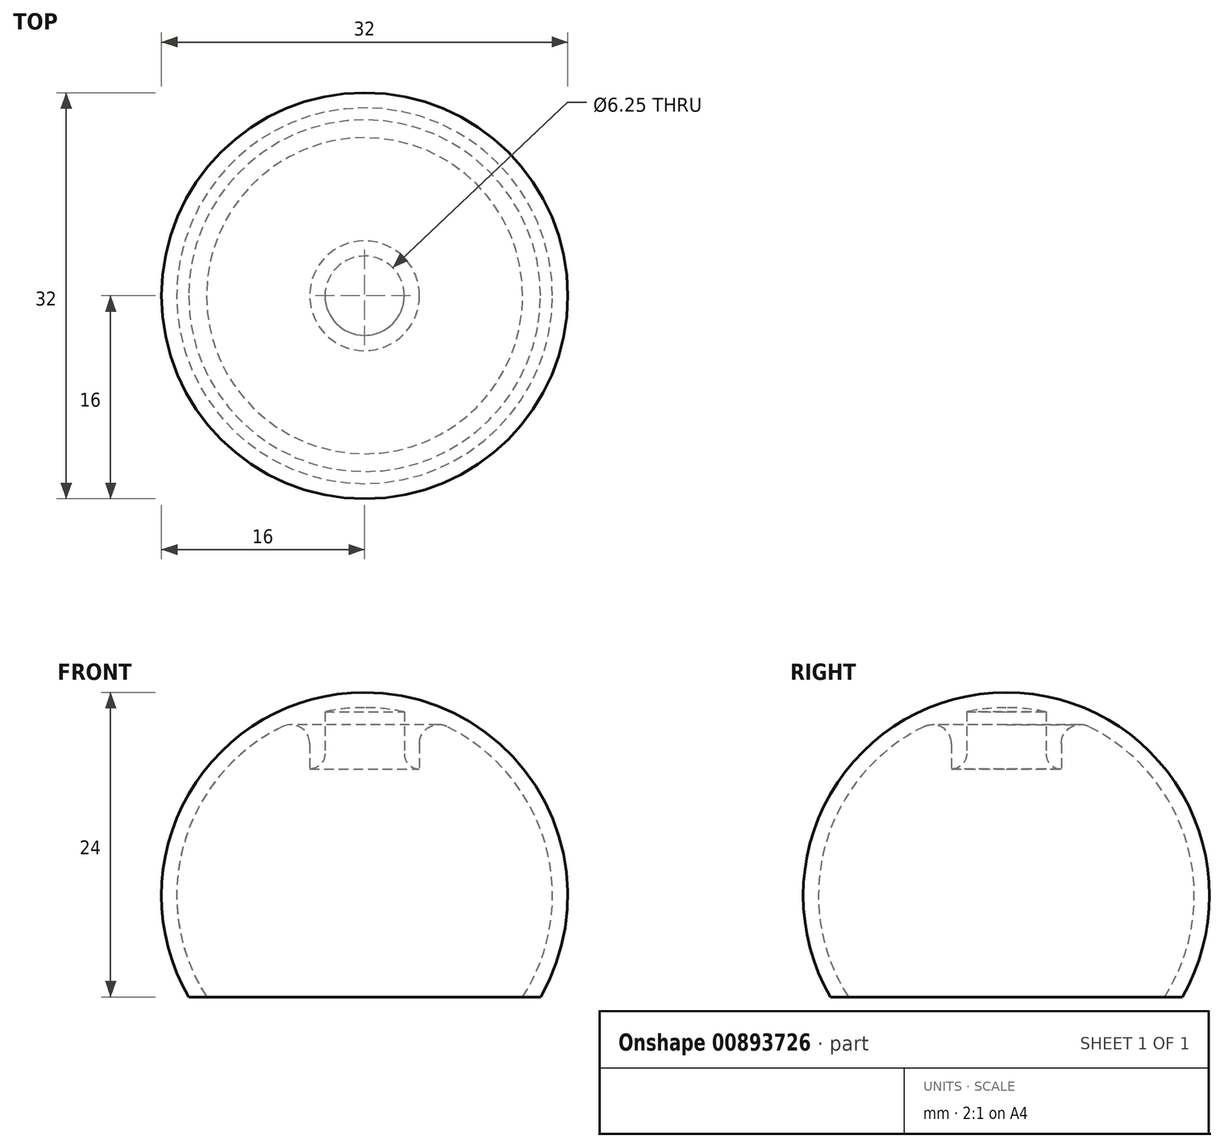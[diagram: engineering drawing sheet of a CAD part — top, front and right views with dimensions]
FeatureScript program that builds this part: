
annotation { "Feature Type Name" : "Feature", "Feature Type Description" : "" }
export const myFeature = defineFeature(function(context is Context, id is Id, definition is map)
    precondition{}
    {
        {
            var Q0;
            Q0=qCreatedBy(makeId("Front.planeOp"),FACE);
            var sketch = newSketch(context, id + "F0", { "sketchPlane" : qUnion([Q0])});
            skArc(sketch, "E0", {"start": v(0, 24) * mm, "mid": v(-13.86, 16) * mm, "end": v(-13.86, 0) * mm});
            skPoint(sketch, "E1", {"position": v(0, 24) * mm});
            skArc(sketch, "E2.0", {"start": v(0, 22.8) * mm, "mid": v(-12.99, 15.1) * mm, "end": v(-12.45, 0) * mm});
            skLineSegment(sketch, "E3", {"start": v(-13.86, 0) * mm, "end": v(-12.45, 0) * mm});
            skPoint(sketch, "E4.orphan", {"position": v(12.45, 0) * mm});
            skPoint(sketch, "E5.orphan", {"position": v(13.86, 0) * mm});
            skLineSegment(sketch, "E6", {"start": v(-4.32, 22.15) * mm, "end": v(-4.32, 17.97) * mm});
            skLineSegment(sketch, "E7", {"start": v(-4.32, 17.97) * mm, "end": v(-3.12, 17.97) * mm});
            skLineSegment(sketch, "E8", {"start": v(-3.12, 17.97) * mm, "end": v(-3.13, 22.47) * mm});
            skLineSegment(sketch, "E9", {"start": v(0, 22.8) * mm, "end": v(0, 24) * mm});
            skSolve(sketch);
        }
        {
            var Q0;
            Q0=qSketchRegion(id+"F0",true);
            var Q1;
            Q1=sQuery(id+"F0.wireOp",EDGE,"E9");
            revolve(context, id + "F1", {"surfaceOperationType" : NewSurfaceOperationType.NEW, "entities" : qUnion([Q0]), "axis" : qUnion([Q1]), "revolveType" : RevolveType.FULL});
        }
        {
            var Q0;
            Q0=makeQuery(id+"F1.opRevolve","SWEPT_EDGE",EDGE,{"disambiguationData":[OSD([sQuery(id+"F0.wireOp",EDGE,"E7"),sQuery(id+"F0.wireOp",EDGE,"E8")])]});
            fillet(context, id + "F2", {"entities" : qUnion([Q0]), "radius" : 1.2 * mm, "tangentPropagation" : true, "allowEdgeOverflow" : false});
        }
        {
            var Q0;
            Q0=makeQuery(id+"F1.opRevolve","SWEPT_EDGE",EDGE,{"disambiguationData":[OSD([sQuery(id+"F0.wireOp",EDGE,"E2.0"),sQuery(id+"F0.wireOp",EDGE,"E6")])]});
            fillet(context, id + "F3", {"entities" : qUnion([Q0]), "radius" : 1.5 * mm, "tangentPropagation" : true, "allowEdgeOverflow" : false});
        }
    });
